FCSTD DOCUMENT  (FreeCAD 1.0R39319 (Git))
Label: wwek2 sketch3
License: All rights reserved
LicenseURL: https://en.wikipedia.org/wiki/All_rights_reserved
objects: Sketcher::SketchObject×1, PartDesign::Body×1, Spreadsheet::Sheet×1
note: 3 computed .brp shape members not serialized (recipe doc carries the construction recipe); baked Part::Feature solids carry a one-line shape summary decoded from their .brp

FEATURE [Sketcher::SketchObject] Sketch
  ArcFitTolerance = 1e-06
  AttachmentSupport = -> [XY_Plane]
  FullyConstrained = false
  MakeInternals = false
  MapMode = 5
  sketch-geometry (53):
    g0: LineSegment StartX=-38.9672 StartY=28.7801 StartZ=0 EndX=-38.9672 EndY=18.7801 EndZ=0
    g1: LineSegment StartX=-38.9672 StartY=18.7801 StartZ=0 EndX=-44.6272 EndY=18.7801 EndZ=0
    g2: LineSegment StartX=-44.6272 StartY=18.7801 StartZ=0 EndX=-44.6272 EndY=23.7901 EndZ=0
    g3: LineSegment StartX=-44.6272 StartY=23.7901 StartZ=0 EndX=-49.7972 EndY=23.7901 EndZ=0
    g4: LineSegment StartX=-49.7972 StartY=23.7901 StartZ=0 EndX=-49.7972 EndY=18.7801 EndZ=0
    g5: LineSegment StartX=-49.7972 StartY=18.7801 StartZ=0 EndX=-55.4572 EndY=18.7801 EndZ=0
    g6: LineSegment StartX=-55.4572 StartY=18.7801 StartZ=0 EndX=-55.4572 EndY=28.7801 EndZ=0
    g7: LineSegment StartX=-55.4572 StartY=28.7801 StartZ=0 EndX=-60.4572 EndY=28.7801 EndZ=0
    g8: LineSegment StartX=-60.4572 StartY=28.7801 StartZ=0 EndX=-60.4572 EndY=53.0012 EndZ=0
    g9: LineSegment StartX=-58.6783 StartY=56.8254 StartZ=0 EndX=-46.86 EndY=66.7801 EndZ=0
    g10: LineSegment StartX=-46.86 StartY=66.7801 StartZ=0 EndX=-43.86 EndY=66.7801 EndZ=0
    g11: LineSegment StartX=-38.9672 StartY=28.7801 StartZ=0 EndX=-33.9672 EndY=28.7801 EndZ=0
    g12: LineSegment StartX=-33.9672 StartY=28.7801 StartZ=0 EndX=-33.9672 EndY=6.78011 EndZ=0
    g13: LineSegment StartX=-33.9672 StartY=6.78011 StartZ=0 EndX=-22.89 EndY=6.78011 EndZ=0
    g14: LineSegment StartX=-22.89 StartY=6.78011 StartZ=0 EndX=-22.89 EndY=-8.21989 EndZ=0
    g15: LineSegment StartX=-22.89 StartY=-8.21989 StartZ=0 EndX=-5.88996 EndY=-8.21989 EndZ=0
    g16: ArcOfCircle CenterX=-55.4572 CenterY=53.0012 CenterZ=0 NormalX=0 NormalY=0 NormalZ=1 AngleXU=0 Radius=5 StartAngle=2.27081 EndAngle=3.14159
    g17: LineSegment StartX=-43.86 StartY=66.7801 StartZ=0 EndX=-43.86 EndY=62.0501 EndZ=0
    g18: LineSegment StartX=-43.86 StartY=62.0501 StartZ=0 EndX=-36.86 EndY=62.0501 EndZ=0
    g19: LineSegment StartX=-36.86 StartY=62.0501 StartZ=0 EndX=-36.86 EndY=58.0501 EndZ=0
    g20: LineSegment StartX=-36.86 StartY=58.0501 StartZ=0 EndX=-28.86 EndY=58.0501 EndZ=0
    g21: LineSegment StartX=-28.86 StartY=58.0501 StartZ=0 EndX=-28.86 EndY=62.0501 EndZ=0
    g22: LineSegment StartX=-28.86 StartY=62.0501 StartZ=0 EndX=-21.86 EndY=62.0501 EndZ=0
    g23: LineSegment StartX=-21.86 StartY=62.0501 StartZ=0 EndX=-21.86 EndY=66.7801 EndZ=0
    g24: LineSegment StartX=-21.86 StartY=66.7801 StartZ=0 EndX=-3.85996 EndY=66.7801 EndZ=0
    g25: LineSegment StartX=-3.85996 StartY=66.7801 StartZ=0 EndX=-3.85996 EndY=52.7801 EndZ=0
    g26: LineSegment StartX=-3.85996 StartY=52.7801 StartZ=0 EndX=-7.85996 EndY=52.7801 EndZ=0
    g27: LineSegment StartX=-7.85996 StartY=52.7801 StartZ=0 EndX=-7.85996 EndY=48.7801 EndZ=0
    g28: LineSegment StartX=-7.85996 StartY=48.7801 StartZ=0 EndX=-3.85996 EndY=48.7801 EndZ=0
    g29: LineSegment StartX=-3.85996 StartY=-6.18989 StartZ=0 EndX=-3.85996 EndY=48.7801 EndZ=0
    g30: ArcOfCircle CenterX=-5.88996 CenterY=-6.18989 CenterZ=0 NormalX=0 NormalY=0 NormalZ=1 AngleXU=0 Radius=2.03 StartAngle=4.71239 EndAngle=6.28319
    g31: ArcOfCircle CenterX=-17 CenterY=37 CenterZ=0 NormalX=0 NormalY=0 NormalZ=1 AngleXU=0 Radius=4.25 StartAngle=2.11632 EndAngle=2.25889
    g32: Circle [constr] CenterX=-17 CenterY=37 CenterZ=0 NormalX=0 NormalY=0 NormalZ=1 AngleXU=0 Radius=3.2
    g33: ArcOfCircle CenterX=-21.25 CenterY=37 CenterZ=0 NormalX=0 NormalY=0 NormalZ=1 AngleXU=0 Radius=1.05 StartAngle=4.83623 EndAngle=7.73014
    g34: ArcOfCircle CenterX=-20.4215 CenterY=39.521 CenterZ=0 NormalX=0 NormalY=0 NormalZ=1 AngleXU=0 Radius=1.05 StartAngle=4.20123 EndAngle=7.09513
    g35: ArcOfCircle CenterX=-18.2472 CenterY=41.0629 CenterZ=0 NormalX=0 NormalY=0 NormalZ=1 AngleXU=0 Radius=1.05 StartAngle=3.56327 EndAngle=6.45717
    g36: ArcOfCircle CenterX=-15.6866 CenterY=41.042 CenterZ=0 NormalX=0 NormalY=0 NormalZ=1 AngleXU=0 Radius=1.05 StartAngle=2.95125 EndAngle=5.84515
    g37: ArcOfCircle CenterX=-13.592 CenterY=39.5393 CenterZ=0 NormalX=0 NormalY=0 NormalZ=1 AngleXU=0 Radius=1.05 StartAngle=2.335 EndAngle=5.2289
    g38: ArcOfCircle CenterX=-12.7505 CenterY=37.0661 CenterZ=0 NormalX=0 NormalY=0 NormalZ=1 AngleXU=0 Radius=1.05 StartAngle=1.7102 EndAngle=4.6041
    g39: ArcOfCircle CenterX=-13.5156 CenterY=34.5666 CenterZ=0 NormalX=0 NormalY=0 NormalZ=1 AngleXU=0 Radius=1.05 StartAngle=1.08501 EndAngle=3.97891
    g40: ArcOfCircle CenterX=-15.5707 CenterY=32.9976 CenterZ=0 NormalX=0 NormalY=0 NormalZ=1 AngleXU=0 Radius=1.05 StartAngle=0.46684 EndAngle=3.36074
    g41: ArcOfCircle CenterX=-18.329 CenterY=32.9631 CenterZ=0 NormalX=0 NormalY=0 NormalZ=1 AngleXU=0 Radius=1.05 StartAngle=6.089 EndAngle=8.9829
    g42: ArcOfCircle CenterX=-20.3699 CenterY=34.4104 CenterZ=0 NormalX=0 NormalY=0 NormalZ=1 AngleXU=0 Radius=1.05 StartAngle=5.49145 EndAngle=8.38535
    g43: ArcOfCircle CenterX=-21.25 CenterY=37 CenterZ=0 NormalX=0 NormalY=0 NormalZ=1 AngleXU=0 Radius=1.05 StartAngle=4.83624 EndAngle=7.73014
    g44: ArcOfCircle CenterX=-17 CenterY=37 CenterZ=0 NormalX=0 NormalY=0 NormalZ=1 AngleXU=0 Radius=4.25 StartAngle=1.5043 EndAngle=1.62094
    g45: ArcOfCircle CenterX=-17 CenterY=37 CenterZ=0 NormalX=0 NormalY=0 NormalZ=1 AngleXU=0 Radius=4.25 StartAngle=0.888051 EndAngle=1.00892
    g46: ArcOfCircle CenterX=-17 CenterY=37 CenterZ=0 NormalX=0 NormalY=0 NormalZ=1 AngleXU=0 Radius=4.25 StartAngle=0.263249 EndAngle=0.392668
    g47: ArcOfCircle CenterX=-17 CenterY=37 CenterZ=0 NormalX=0 NormalY=0 NormalZ=1 AngleXU=0 Radius=4.25 StartAngle=5.92124 EndAngle=6.05105
    g48: ArcOfCircle CenterX=-17 CenterY=37 CenterZ=0 NormalX=0 NormalY=0 NormalZ=1 AngleXU=0 Radius=4.25 StartAngle=5.30307 EndAngle=5.42586
    g49: ArcOfCircle CenterX=-17 CenterY=37 CenterZ=0 NormalX=0 NormalY=0 NormalZ=1 AngleXU=0 Radius=4.25 StartAngle=4.64205 EndAngle=4.80769
    g50: ArcOfCircle CenterX=-17 CenterY=37 CenterZ=0 NormalX=0 NormalY=0 NormalZ=1 AngleXU=0 Radius=4.25 StartAngle=4.0445 EndAngle=4.14667
    g51: ArcOfCircle CenterX=-17 CenterY=37 CenterZ=0 NormalX=0 NormalY=0 NormalZ=1 AngleXU=0 Radius=4.25 StartAngle=3.38928 EndAngle=3.54911
    g52: ArcOfCircle CenterX=-17 CenterY=37 CenterZ=0 NormalX=0 NormalY=0 NormalZ=1 AngleXU=0 Radius=4.25 StartAngle=2.75427 EndAngle=2.8939
  constraints (154):
    c: Vertical(g0)
    c: Coincident(g0,g1)
    c: Horizontal(g1)
    c: Coincident(g1,g2)
    c: Vertical(g2)
    c: Coincident(g2,g3)
    c: Horizontal(g3)
    c: Coincident(g3,g4)
    c: Vertical(g4)
    c: Coincident(g4,g5)
    c: Horizontal(g5)
    c: Coincident(g5,g6)
    c: Vertical(g6)
    c: DistanceY(g6,g6) = 10
    c: Equal(g6,g0)
    c: Equal(g4,g2)
    c: Equal(g5,g1)
    c: Coincident(g6,g7)
    c: Horizontal(g7)
    c: Coincident(g7,g8)
    c: Vertical(g8)
    c: Coincident(g9,g10)
    c: DistanceX(g7,g7) = 5
    c: Coincident(g0,g11)
    c: Horizontal(g11)
    c: Coincident(g11,g12)
    c: Vertical(g12)
    c: DistanceY(g4,g4) = 5.01
    c: DistanceX(g5,g5) = 5.66
    c: DistanceX(g3,g3) = 5.17
    c: DistanceX(g11,g11) = 5
    c: Coincident(g12,g13)
    c: Horizontal(g13)
    c: Coincident(g13,g14)
    c: Vertical(g14)
    c: Coincident(g14,g15)
    c: Horizontal(g15)
    c: Distance(g13,g11) = 22
    c: Distance(g15,g13) = 15
    c: Tangent(g9,g16) = 1.5708
    c: Tangent(g8,g16) = 1.5708
    c: Radius(g16) = 5
    c: Distance(g10,g10) = 3
    c: Coincident(g10,g17)
    c: Vertical(g17)
    c: Coincident(g17,g18)
    c: Horizontal(g18)
    c: Coincident(g18,g19)
    c: Vertical(g19)
    c: Coincident(g19,g20)
    c: Horizontal(g20)
    c: Coincident(g20,g21)
    c: Vertical(g21)
    c: Coincident(g21,g22)
    c: Horizontal(g22)
    c: Coincident(g22,g23)
    c: Vertical(g23)
    c: Coincident(g23,g24)
    c: Horizontal(g24)
    c: Coincident(g24,g25)
    c: Vertical(g25)
    c: Coincident(g25,g26)
    c: Horizontal(g26)
    c: Coincident(g26,g27)
    c: Vertical(g27)
    c: Coincident(g27,g28)
    c: Horizontal(g28)
    c: DistanceX(g24,g24) = 18
    c: Coincident(g29,g28)
    c: Vertical(g29)
    c: Distance(g21,g19) = 8
    c: DistanceY(g19,g19) = 4
    c: Equal(g19,g21)
    c: Equal(g18,g22)
    c: Equal(g17,g23)
    c: DistanceY(g17,g17) = 4.73
    c: Distance(g23,g17) = 22
    c: Distance(g28,g26) = 4
    c: DistanceX(g26,g26) = 4
    c: Equal(g26,g28)
    c: Distance(g15,g28) = 57
    c: DistanceY(g25,g25) = 14
    c: Block(g10)
    c: Distance(g9,g15) = 75
    c: Block(g9)
    c: Block(g16)
    c: Block(g8)
    c: Tangent(g29,g30) = -1.5708
    c: Tangent(g15,g30) = -1.5708
    c: Radius(g30) = 2.03
    c: DistanceX(g15,g15) = 17
    c: Diameter(g31) = 8.5
    c: Diameter(g32) = 6.4
    c: Tangent(g33,g32)
    c: PointOnObject(g33,g51)
    c: PointOnObject(g33,g52)
    c: PointOnObject(g34,g52)
    c: PointOnObject(g34,g31)
    c: PointOnObject(g35,g31)
    c: PointOnObject(g36,g44)
    c: PointOnObject(g36,g31)
    c: PointOnObject(g37,g45)
    c: PointOnObject(g37,g31)
    c: PointOnObject(g38,g46)
    c: PointOnObject(g38,g31)
    c: PointOnObject(g39,g47)
    c: PointOnObject(g39,g31)
    c: PointOnObject(g40,g48)
    c: PointOnObject(g40,g49)
    c: PointOnObject(g41,g49)
    c: PointOnObject(g41,g50)
    c: PointOnObject(g42,g50)
    c: PointOnObject(g42,g51)
    c: Equal(g33, g34-g42) x9
    c: Coincident(g44,g35)
    c: Coincident(g31,g35)
    c: Equal(g31,g44)
    c: Coincident(g45,g36)
    c: PointOnObject(g44,g36)
    c: Coincident(g31,g44)
    c: Equal(g31,g45)
    c: Coincident(g46,g37)
    c: PointOnObject(g45,g37)
    c: Coincident(g31,g45)
    c: Equal(g31,g46)
    c: Coincident(g47,g38)
    c: PointOnObject(g46,g38)
    c: Coincident(g31,g46)
    c: Equal(g31,g47)
    c: Coincident(g48,g39)
    c: PointOnObject(g47,g39)
    c: Coincident(g31,g47)
    c: Equal(g31,g48)
    c: Coincident(g49,g40)
    c: PointOnObject(g48,g40)
    c: Coincident(g31,g48)
    c: Equal(g31,g49)
    c: Coincident(g50,g41)
    c: PointOnObject(g49,g41)
    c: Coincident(g31,g49)
    c: Equal(g31,g50)
    c: Coincident(g51,g42)
    c: PointOnObject(g50,g42)
    c: Coincident(g31,g50)
    c: Equal(g31,g51)
    c: PointOnObject(g51,g33)
    c: Coincident(g31,g51)
    c: Coincident(g52,g33)
    c: Equal(g31,g52)
    c: Coincident(g31,g34)
    c: PointOnObject(g52,g34)
    c: Coincident(g31,g52)
    c: Block(g37)
    c: Block(g32)
FEATURE [PartDesign::Body] Body
  AllowCompound = false
  Group = -> [Sketch]
  Origin = -> Origin
FEATURE [Spreadsheet::Sheet] Spreadsheet
  cells = A1='siderec; B1(siderec)=10; A2='sidedist; B2(sidedist)=5; A3='rightdist; B3(rightdist)=4; A4='siderectobottom; B4(siderectobottom)=22; A5='bootomside; B5(bootomside)=21; A6='midtobottom; B6(midtobottom)=15; A7='moredeep; B7(moredeep)=17; A8='fillet; B8(fillet)=2; A9='bottomtoup; B9(bottomtoup)=57; A10='square; B10(square)=17; A11='squaretoup; B11(squaretoup)=14; A12='rightleft; B12(rightleft)=18; A13='midsquare; B13(midsquare)=8; A14='square1; B14(square1)=4; A15='incline; B15(incline)=3; A16='arc; B16(arc)=5; A17='arctobotoom; B17(arctobotoom)=75
